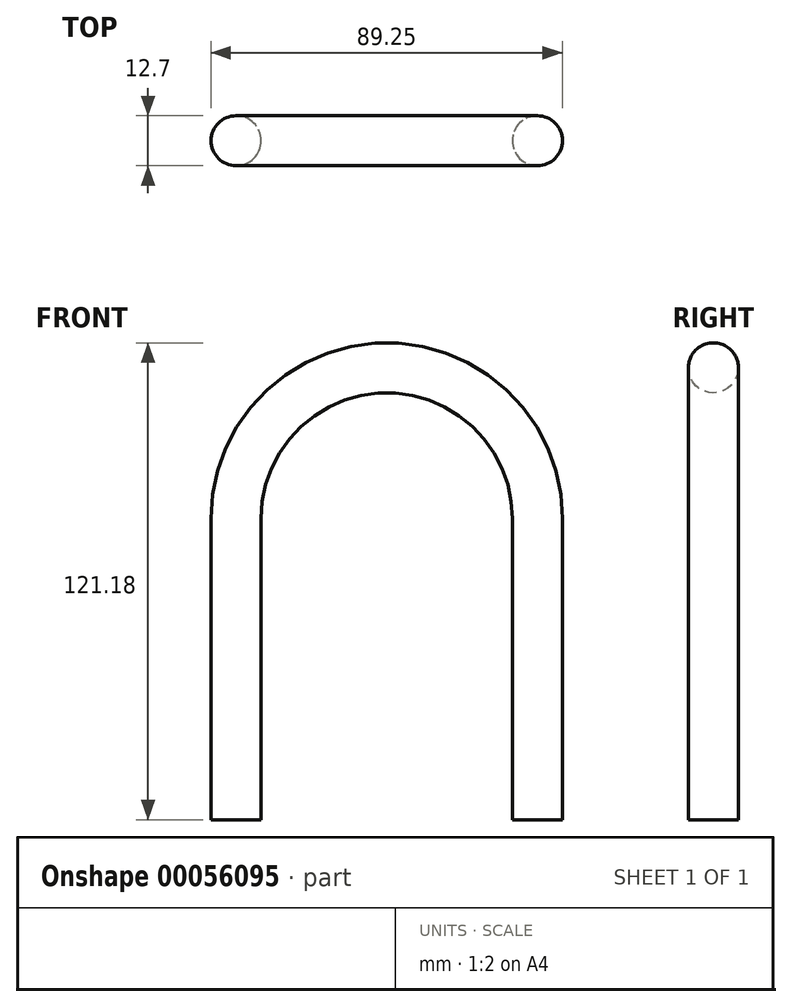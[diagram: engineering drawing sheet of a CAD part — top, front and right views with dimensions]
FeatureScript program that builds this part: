
annotation { "Feature Type Name" : "Feature", "Feature Type Description" : "" }
export const myFeature = defineFeature(function(context is Context, id is Id, definition is map)
    precondition{}
    {
        {
            var Q0;
            Q0=qCreatedBy(makeId("Front.planeOp"),FACE);
            var sketch = newSketch(context, id + "F0", { "sketchPlane" : qUnion([Q0])});
            skLineSegment(sketch, "E0", {"start": v(0, 0) * mm, "end": v(0, 76.56) * mm});
            skLineSegment(sketch, "E1", {"start": v(-76.55, 0) * mm, "end": v(-76.55, 76.56) * mm});
            skArc(sketch, "E2", {"start": v(-76.55, 76.56) * mm, "mid": v(-38.27, 114.83) * mm, "end": v(0, 76.56) * mm});
            skSolve(sketch);
        }
        {
            var Q0;
            Q0=qCreatedBy(makeId("Top.planeOp"),FACE);
            var sketch = newSketch(context, id + "F1", { "sketchPlane" : qUnion([Q0])});
            skCircle(sketch, "E3", {"center": v(0, 0) * mm, "radius": 6.35 * mm});
            skCircle(sketch, "E4", {"center": v(-76.55, 0) * mm, "radius": 6.35 * mm});
            skSolve(sketch);
        }
        {
            var Q0;
            Q0=makeQuery(id+"F1.imprint","IMPRINT",FACE,{"disambiguationData":[TD([[makeQuery(id+"F1.imprint","IMPRINT",EDGE,{"derivedFrom":sQuery(id+"F1.wireOp",EDGE,"E3")}),1.0]])]});
            var Q1;
            Q1=sQuery(id+"F0.wireOp",EDGE,"E0");
            var Q2;
            Q2=sQuery(id+"F0.wireOp",EDGE,"E2");
            var Q3;
            Q3=sQuery(id+"F0.wireOp",EDGE,"E1");
            sweep(context, id + "F2", {"profiles" : qUnion([Q0]), "path" : qUnion([Q1, Q2, Q3])});
        }
    });
